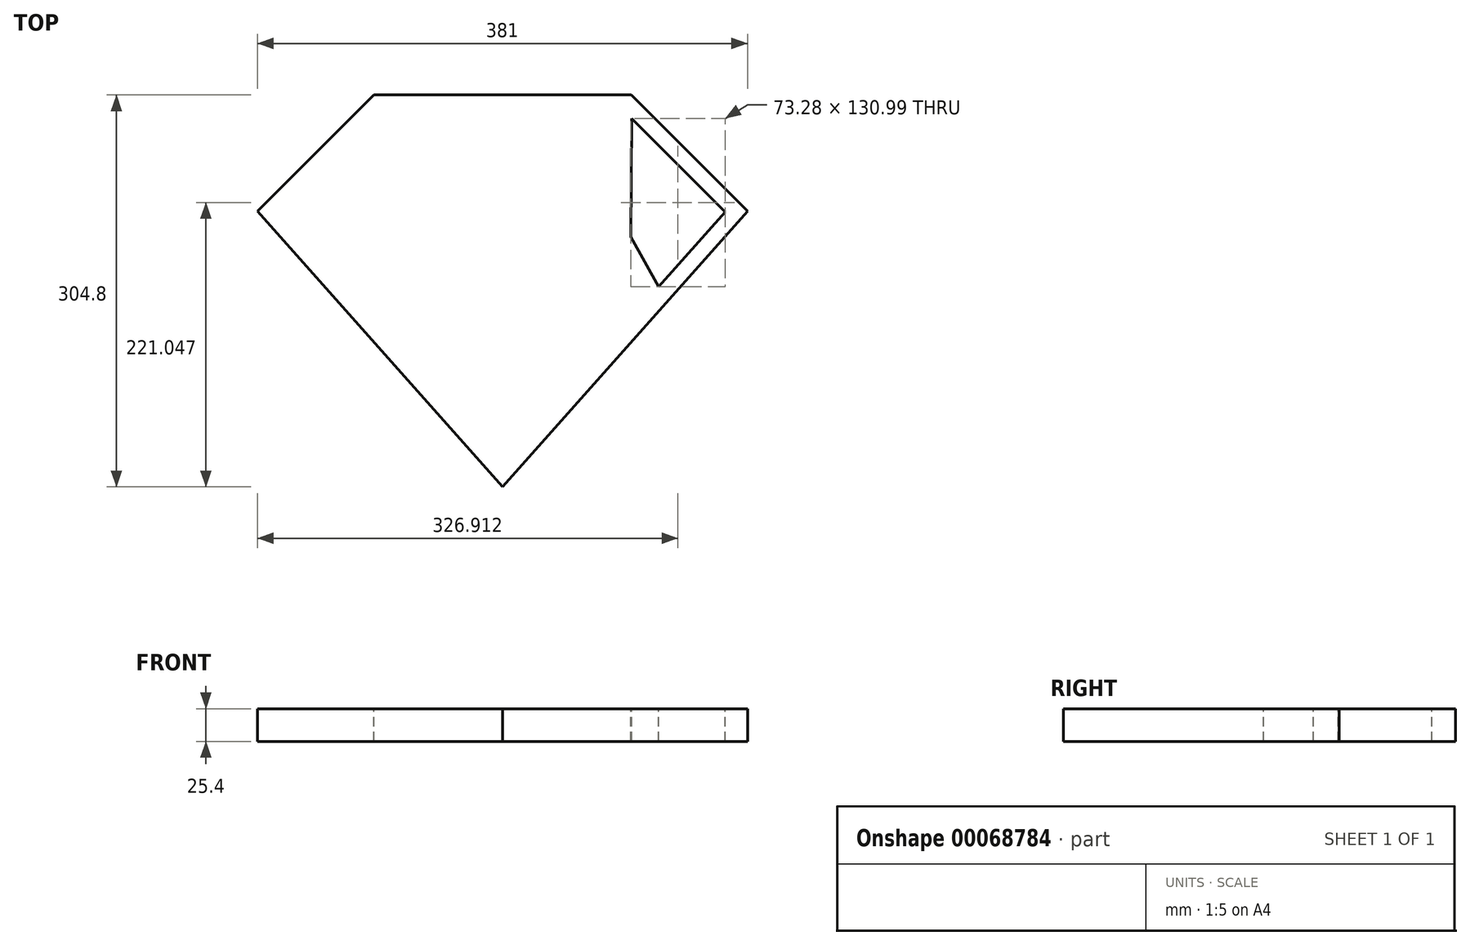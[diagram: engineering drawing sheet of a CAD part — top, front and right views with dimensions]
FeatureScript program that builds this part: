
annotation { "Feature Type Name" : "Feature", "Feature Type Description" : "" }
export const myFeature = defineFeature(function(context is Context, id is Id, definition is map)
    precondition{}
    {
        {
            var Q0;
            Q0=qCreatedBy(makeId("Top.planeOp"),FACE);
            var sketch = newSketch(context, id + "F0", { "sketchPlane" : qUnion([Q0])});
            skLineSegment(sketch, "E0.rect.bottom", {"start": v(190.5, 152.4) * mm, "end": v(-190.5, 152.4) * mm});
            skLineSegment(sketch, "E0.rect.top", {"start": v(190.5, -152.4) * mm, "end": v(-190.5, -152.4) * mm});
            skLineSegment(sketch, "E0.rect.left", {"start": v(190.5, 152.4) * mm, "end": v(190.5, -152.4) * mm});
            skLineSegment(sketch, "E0.rect.right", {"start": v(-190.5, 152.4) * mm, "end": v(-190.5, -152.4) * mm});
            skPoint(sketch, "E0.rect.middle", {"position": v(0, 0) * mm});
            skSolve(sketch);
        }
        {
            var Q0;
            Q0=makeQuery(id+"F0.imprint","IMPRINT",FACE,{"disambiguationData":[TD([[makeQuery(id+"F0.imprint","IMPRINT",EDGE,{"derivedFrom":sQuery(id+"F0.wireOp",EDGE,"E0.rect.bottom")}),1.0]])]});
            extrude(context, id + "F1", {"entities" : qUnion([Q0]), "depth" : 25.4 * mm});
        }
        {
            var Q0;
            Q0=makeQuery(id+"F1.opExtrude","CAP_FACE",FACE,{"disambiguationData":[OSD([sQuery(id+"F0.wireOp",EDGE,"E0.rect.bottom"),sQuery(id+"F0.wireOp",EDGE,"E0.rect.top"),sQuery(id+"F0.wireOp",EDGE,"E0.rect.left"),sQuery(id+"F0.wireOp",EDGE,"E0.rect.right")])],"isStart":false});
            var sketch = newSketch(context, id + "F2", { "sketchPlane" : qUnion([Q0])});
            skLineSegment(sketch, "E1", {"start": v(-190.5, 61.93) * mm, "end": v(-100.03, 152.4) * mm});
            skLineSegment(sketch, "E2", {"start": v(-190.5, 61.93) * mm, "end": v(0, -152.4) * mm});
            skLineSegment(sketch, "E3", {"start": v(0, -152.4) * mm, "end": v(0, 152.4) * mm});
            skLineSegment(sketch, "E4", {"start": v(0, 152.4) * mm, "end": v(-100.03, 152.4) * mm});
            skLineSegment(sketch, "E5", {"start": v(-100.03, 152.4) * mm, "end": v(-190.5, 152.4) * mm});
            skLineSegment(sketch, "E6", {"start": v(-190.5, 152.4) * mm, "end": v(-190.5, 61.93) * mm});
            skLineSegment(sketch, "E7", {"start": v(-190.5, 61.93) * mm, "end": v(-190.5, -152.4) * mm});
            skLineSegment(sketch, "E8", {"start": v(-190.5, -152.4) * mm, "end": v(0, -152.4) * mm});
            skSolve(sketch);
        }
        {
            var Q0;
            Q0=makeQuery(id+"F2.imprint","IMPRINT",FACE,{"disambiguationData":[TD([[makeQuery(id+"F2.imprint","IMPRINT",EDGE,{"derivedFrom":sQuery(id+"F2.wireOp",EDGE,"E1")}),1.0]])]});
            var Q1;
            Q1=makeQuery(id+"F2.imprint","IMPRINT",FACE,{"disambiguationData":[TD([[makeQuery(id+"F2.imprint","IMPRINT",EDGE,{"derivedFrom":sQuery(id+"F2.wireOp",EDGE,"E2")}),-1.0]])]});
            extrude(context, id + "F3", {"entities" : qUnion([Q0, Q1]), "operationType" : NewBodyOperationType.REMOVE, "oppositeDirection" : true, "depth" : 25.4 * mm});
        }
        {
            var Q0;
            Q0=makeQuery(id+"F1.opExtrude","SWEPT_BODY",BODY,{"disambiguationData":[OSD([sQuery(id+"F0.wireOp",EDGE,"E0.rect.bottom"),sQuery(id+"F0.wireOp",EDGE,"E0.rect.top"),sQuery(id+"F0.wireOp",EDGE,"E0.rect.left"),sQuery(id+"F0.wireOp",EDGE,"E0.rect.right")])]});
            var Q1;
            Q1=qCreatedBy(makeId("Right.planeOp"),FACE);
            mirror(context, id + "F4", {"operationType" : NewBodyOperationType.INTERSECT, "entities" : qUnion([Q0]), "mirrorPlane" : qUnion([Q1])});
        }
        {
            var Q0;
            Q0=makeQuery(id+"F1.opExtrude","CAP_FACE",FACE,{"disambiguationData":[OSD([sQuery(id+"F0.wireOp",EDGE,"E0.rect.bottom"),sQuery(id+"F0.wireOp",EDGE,"E0.rect.top"),sQuery(id+"F0.wireOp",EDGE,"E0.rect.left"),sQuery(id+"F0.wireOp",EDGE,"E0.rect.right")])],"isStart":false});
            var sketch = newSketch(context, id + "F5", { "sketchPlane" : qUnion([Q0])});
            skLineSegment(sketch, "E9", {"start": v(100.33, 134.14) * mm, "end": v(173.05, 61.42) * mm});
            skLineSegment(sketch, "E10", {"start": v(173.05, 61.42) * mm, "end": v(121.26, 3.15) * mm});
            skLineSegment(sketch, "E11", {"start": v(121.26, 3.15) * mm, "end": v(99.77, 41.84) * mm});
            skLineSegment(sketch, "E12", {"start": v(99.77, 41.84) * mm, "end": v(100.33, 134.14) * mm});
            skSolve(sketch);
        }
        {
            var Q0;
            Q0=makeQuery(id+"F5.imprint","IMPRINT",FACE,{"disambiguationData":[TD([[makeQuery(id+"F5.imprint","IMPRINT",EDGE,{"derivedFrom":sQuery(id+"F5.wireOp",EDGE,"E9")}),-1.0]])]});
            extrude(context, id + "F6", {"entities" : qUnion([Q0]), "operationType" : NewBodyOperationType.REMOVE, "endBound" : BoundingType.THROUGH_ALL, "oppositeDirection" : true, "depth" : 25.4 * mm});
        }
    });
